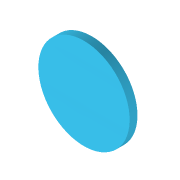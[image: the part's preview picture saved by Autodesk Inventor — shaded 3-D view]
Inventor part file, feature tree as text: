
AUTODESK INVENTOR PART (.ipt)
format: ipt  version: 2022 (Build 260153000, 153)  size: 140,288 bytes
history: native  units: mm
features: reference x6, other x2, revolve x1, sketch x1
ambient origin geometry x8: Origin, YZ Plane, XZ Plane, XY Plane, X Axis, Y Axis, Z Axis, Center Point
bodies: Volumenkörper1 (feature_tree)
feature tree (10):
  revolve  "Umdrehung1"
  sketch  "Skizze1"  dims[d0=5.0mm d1=3.0mm d2=17.101639mm d3=8.550819mm d4=12.0mm d5=0.2mm d6=6.1mm d7=360.0deg]
  reference  "Referenz1"
  reference  "Referenz2"
  reference  "Referenz3"
  reference  "Referenz4"
  reference  "Referenz5"
  reference  "Referenz6"
  other  "50_Assembly_ETL_Mould.iam"
  other  "50_ETL_Membrane_v0:1"
